annotation { "Feature Type Name" : "Feature", "Feature Type Description" : "" }
export const myFeature = defineFeature(function(context is Context, id is Id, definition is map)
    precondition{}
    {
        {
            var Q0;
            Q0=qCreatedBy(makeId("Top.planeOp"),FACE);
            var sketch = newSketch(context, id + "F0", { "sketchPlane" : qUnion([Q0])});
            skLineSegment(sketch, "E0.bottom", {"start": v(87.5, -50) * mm, "end": v(-62.5, -50) * mm});
            skLineSegment(sketch, "E0.top", {"start": v(87.5, 50) * mm, "end": v(-62.5, 50) * mm});
            skLineSegment(sketch, "E0.left", {"start": v(87.5, -50) * mm, "end": v(87.5, 50) * mm});
            skLineSegment(sketch, "E0.right", {"start": v(-87.5, -20) * mm, "end": v(-87.5, 20) * mm});
            skPoint(sketch, "E0.middle", {"position": v(0, 0) * mm});
            skPoint(sketch, "E1", {"position": v(-87.5, 20) * mm});
            skPoint(sketch, "E2", {"position": v(-62.5, 50) * mm});
            skArc(sketch, "E3", {"start": v(-87.5, 20) * mm, "mid": v(-72.08, 32.56) * mm, "end": v(-62.5, 50) * mm});
            skLineSegment(sketch, "E4", {"start": v(-87.5, 0) * mm, "end": v(87.5, 0) * mm, "construction": true});
            skArc(sketch, "E5.MirrorCS", {"start": v(-87.5, -20) * mm, "mid": v(-72.08, -32.56) * mm, "end": v(-62.5, -50) * mm});
            skPoint(sketch, "E6.orphan", {"position": v(-87.5, 50) * mm});
            skPoint(sketch, "E7.orphan", {"position": v(-87.5, -50) * mm});
            skSolve(sketch);
        }
        {
            var Q0;
            Q0=qSketchRegion(id+"F0",true);
            extrude(context, id + "F1", {"entities" : qUnion([Q0]), "depth" : 3 * mm, "offsetDistance" : 25 * mm});
        }
        {
            var Q0;
            {var subQ0=sQuery(id+"F0.wireOp",EDGE,"E3");var subQ1=sQuery(id+"F0.wireOp",EDGE,"E0.left");var subQ2=sQuery(id+"F0.wireOp",EDGE,"E0.top");var subQ3=sQuery(id+"F0.wireOp",EDGE,"E0.bottom");var subQ4=sQuery(id+"F0.wireOp",EDGE,"E5.MirrorCS");Q0=makeQuery(id+"FjsPoqis3ipD7dL_1.boolean.opBoolean","SPLIT",FACE,{"disambiguationData":[TD([makeQuery(id+"F1.opExtrude","SWEPT_FACE",FACE,{"disambiguationData":[OSD([subQ3])]})])],"derivedFrom":makeQuery(id+"F1.opExtrude","CAP_FACE",FACE,{"disambiguationData":[OSD([subQ3,subQ2,subQ1,sQuery(id+"F0.wireOp",EDGE,"E0.right"),subQ0,subQ4])],"isStart":false})});}
            var sketch = newSketch(context, id + "F2", { "sketchPlane" : qUnion([Q0])});
            skText(sketch, "E8", { "text": "ibTECHar", "fontName": "OpenSans-Bold.ttf"});
            skLineSegment(sketch, "E9.bottom", {"start": v(5.5, 45.5) * mm, "end": v(25.5, 45.5) * mm});
            skLineSegment(sketch, "E9.top", {"start": v(5.5, 25.5) * mm, "end": v(25.5, 25.5) * mm});
            skLineSegment(sketch, "E9.left", {"start": v(5.5, 45.5) * mm, "end": v(5.5, 25.5) * mm});
            skLineSegment(sketch, "E9.right", {"start": v(25.5, 45.5) * mm, "end": v(25.5, 25.5) * mm});
            skLineSegment(sketch, "E10", {"start": v(35.5, 26.68) * mm, "end": v(55.5, 26.68) * mm});
            skLineSegment(sketch, "E11", {"start": v(55.5, 26.68) * mm, "end": v(45.5, 44) * mm});
            skLineSegment(sketch, "E12", {"start": v(45.5, 44) * mm, "end": v(35.5, 26.68) * mm});
            skCircle(sketch, "E13", {"center": v(67.25, 36) * mm, "radius": 10 * mm});
            skCircle(sketch, "E14", {"center": v(-59.56, 16.57) * mm, "radius": 5 * mm});
            skCircle(sketch, "E15.1.0.0", {"center": v(-47.06, 16.57) * mm, "radius": 5 * mm});
            skCircle(sketch, "E15.2.0.0", {"center": v(-34.56, 16.57) * mm, "radius": 5 * mm});
            skCircle(sketch, "E15.3.0.0", {"center": v(-22.06, 16.57) * mm, "radius": 5 * mm});
            skCircle(sketch, "E15.4.0.0", {"center": v(-9.56, 16.57) * mm, "radius": 5 * mm});
            skCircle(sketch, "E15.5.0.0", {"center": v(2.94, 16.57) * mm, "radius": 5 * mm});
            skCircle(sketch, "E15.6.0.0", {"center": v(15.44, 16.57) * mm, "radius": 5 * mm});
            skCircle(sketch, "E15.7.0.0", {"center": v(27.94, 16.57) * mm, "radius": 5 * mm});
            skCircle(sketch, "E15.8.0.0", {"center": v(40.44, 16.57) * mm, "radius": 5 * mm});
            skCircle(sketch, "E15.9.0.0", {"center": v(52.94, 16.57) * mm, "radius": 5 * mm});
            skCircle(sketch, "E15.10.0.0", {"center": v(65.44, 16.57) * mm, "radius": 5 * mm});
            skCircle(sketch, "E15.11.0.0", {"center": v(77.94, 16.57) * mm, "radius": 5 * mm});
            skLineSegment(sketch, "E15.direction1", {"start": v(-59.56, 11.57) * mm, "end": v(-47.06, 11.57) * mm, "construction": true});
            skText(sketch, "E16", { "text": "ABCDEFGHIJKLMNOPQ", "fontName": "OpenSans-Bold.ttf"});
            skText(sketch, "E17", { "text": "RSTUV WXYZ", "fontName": "OpenSans-Bold.ttf"});
            skText(sketch, "E18", { "text": "abcdefghijklmnopq", "fontName": "OpenSans-Bold.ttf"});
            skText(sketch, "E19", { "text": "rstuvwxyz", "fontName": "OpenSans-Bold.ttf"});
            skCircle(sketch, "E20", {"center": v(79.71, -37.38) * mm, "radius": 5 * mm});
            skCircle(sketch, "E21", {"center": v(-56.96, -37.38) * mm, "radius": 5 * mm});
            const initialGuessF2  = {"E8": [-0.06595, 0.02657, 1, 0, 0.011], "E16": [-0.06049, -0.00125, 1, 0, 0.009], "E17": [-0.03082, -0.01365, 1, 0, 0.0091], "E18": [-0.0546, -0.02653, 1, 0, 0.00972], "E19": [-0.02796, -0.04027, 1, 0, 0.01051]};
            skSetInitialGuess(sketch, initialGuessF2);
            skSolve(sketch);
        }
        {
            var Q0;
            Q0=qSketchRegion(id+"F2",true);
            extrude(context, id + "F3", {"entities" : qUnion([Q0]), "operationType" : NewBodyOperationType.REMOVE, "oppositeDirection" : true, "depth" : 25 * mm, "offsetDistance" : 25 * mm});
        }
    });